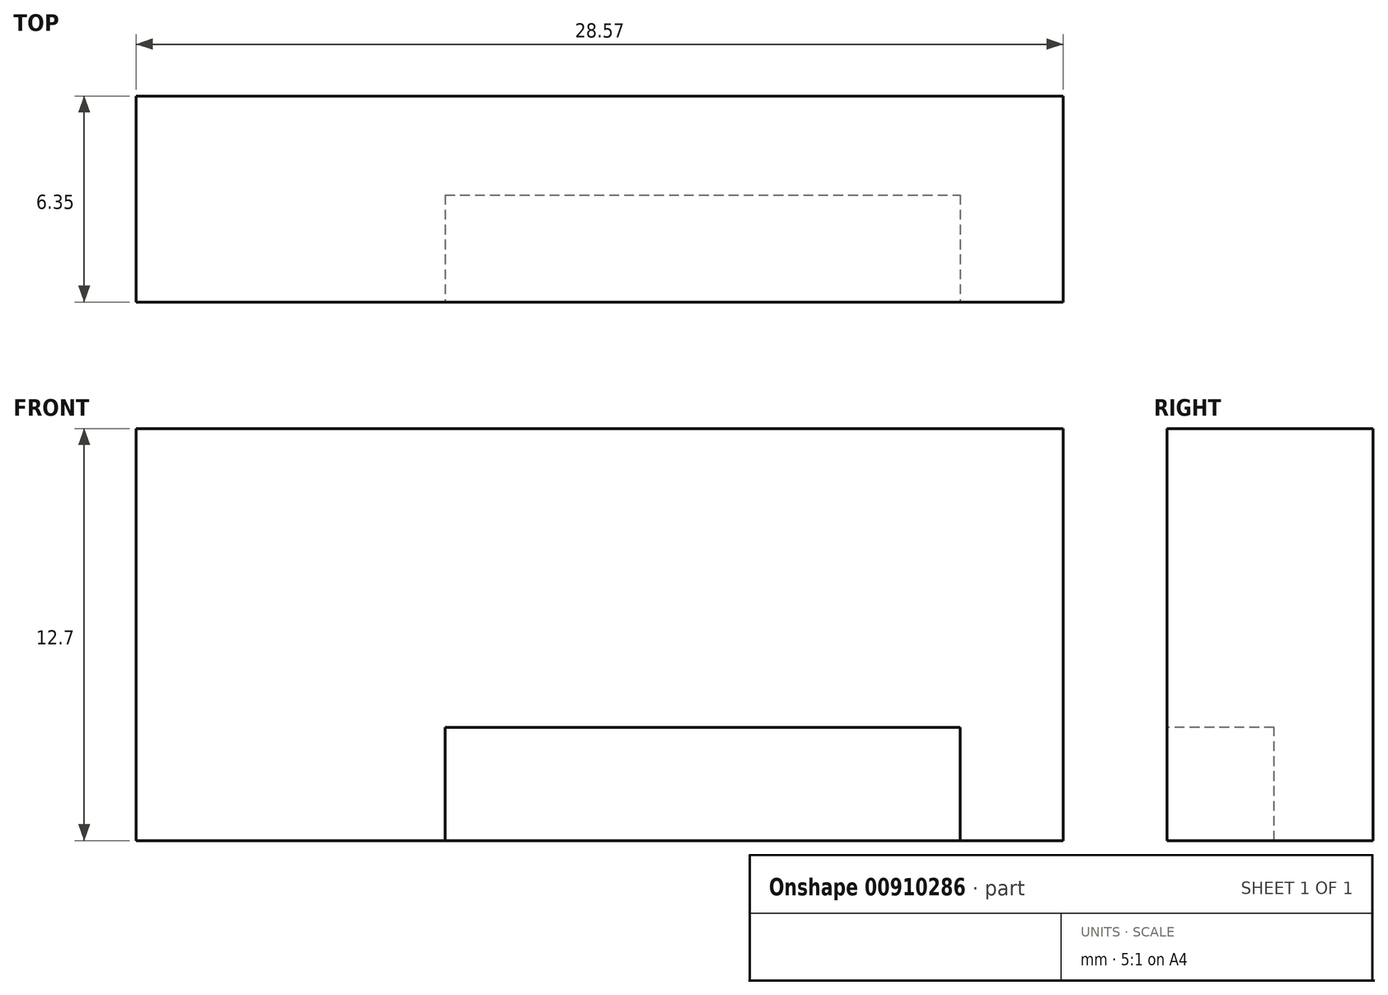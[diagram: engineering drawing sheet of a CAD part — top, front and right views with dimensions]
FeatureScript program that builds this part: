
annotation { "Feature Type Name" : "Feature", "Feature Type Description" : "" }
export const myFeature = defineFeature(function(context is Context, id is Id, definition is map)
    precondition{}
    {
        {
            var Q0;
            Q0=qCreatedBy(makeId("Front.planeOp"),FACE);
            var sketch = newSketch(context, id + "F0", { "sketchPlane" : qUnion([Q0])});
            skLineSegment(sketch, "E0.bottom", {"start": v(0, 0) * mm, "end": v(28.58, 0) * mm});
            skLineSegment(sketch, "E0.top", {"start": v(0, 12.7) * mm, "end": v(28.58, 12.7) * mm});
            skLineSegment(sketch, "E0.left", {"start": v(0, 0) * mm, "end": v(0, 12.7) * mm});
            skLineSegment(sketch, "E0.right", {"start": v(28.58, 0) * mm, "end": v(28.58, 12.7) * mm});
            skSolve(sketch);
        }
        {
            var Q0;
            Q0 = qSketchRegion(id + "F0", true);
            extrude(context, id + "F1", {"entities" : qUnion([Q0]), "depth" : 6.35 * mm, "offsetDistance" : 25.4 * mm});
        }
        {
            var Q0;
            Q0=makeQuery(id+"F1.opExtrude","CAP_FACE",FACE,{"disambiguationData":[OSD([sQuery(id+"F0.wireOp",EDGE,"E0.bottom"),sQuery(id+"F0.wireOp",EDGE,"E0.top"),sQuery(id+"F0.wireOp",EDGE,"E0.left"),sQuery(id+"F0.wireOp",EDGE,"E0.right")])],"isStart":false});
            var sketch = newSketch(context, id + "F2", { "sketchPlane" : qUnion([Q0])});
            skLineSegment(sketch, "E1.bottom", {"start": v(25.4, 0) * mm, "end": v(9.53, 0) * mm});
            skLineSegment(sketch, "E1.top", {"start": v(25.4, 3.5) * mm, "end": v(9.53, 3.5) * mm});
            skLineSegment(sketch, "E1.left", {"start": v(25.4, 0) * mm, "end": v(25.4, 3.5) * mm});
            skLineSegment(sketch, "E1.right", {"start": v(9.53, 0) * mm, "end": v(9.53, 3.5) * mm});
            skLineSegment(sketch, "E2", {"start": v(6.35, 0) * mm, "end": v(6.35, 6.4) * mm, "construction": true});
            skSolve(sketch);
        }
        {
            var Q0;
            Q0 = qSketchRegion(id + "F2", true);
            extrude(context, id + "F3", {"entities" : qUnion([Q0]), "operationType" : NewBodyOperationType.REMOVE, "oppositeDirection" : true, "depth" : 3.3 * mm, "offsetDistance" : 25.4 * mm});
        }
    });
